# Revit family: FT Round Adjustable
name_source: partatom
category: Lighting Fixtures
revit_build: Autodesk Revit 2018 (Build: 20170927_1515(x64)
units: mm (PartAtom-declared; Revit-internal decimal feet)

## family parameters
Always vertical = Yes
Cut with Voids When Loaded = No
Host = Ceiling
Light Source = Yes
OmniClass Number = 23.80.70.11
OmniClass Title = Luminaries for Internal Lighting
Part Type = Normal
Room Calculation Point = No
Round Connector Dimension = Use Diameter
Shared = No

## types (2) — shared parameters
Color Filter = 16777215
Dimming Lamp Color Temperature Shift = <None>
Manufacturer URL - Europe and Rest of World = www.astrolighting.com
Manufacturer URL - North America = us.astrolighting.com
zero-valued in all types: Product Weight (KG)

## per-type parameters (varying)
| type | ADA compliant | Dimmable | Dimming Method | Driver Included | Driver Required | Efficacy (lm/w) | Electrical Class | Lamp | Length of supplied cable | Light Source Fixed | Location / IP Rating | Main Finish | Main Material | Photometric Web File | Power (Watts) | Product CCT | Product CRI | Product Location | Product Name | Product SKU | Tilt Angle |
| CE | Not Applicable | Yes | Control Gear Dependent | No | Yes | 72 | III | COB LED | 450mm | Yes | IP20 | White | Aluminium | Minima Round Fixed ALT LED Module.ies | 13.8 | 3000K | 90 | Indoor | Proform FT Round Adjustable | 1243005 | 30.00° |
| ETL |  |  |  |  |  |  |  |  |  |  |  |  |  | generic |  | 2700K / 3000K | 80/ 90 |  |  | 1234567 | 60.00° |

## geometry (parser evidence)
native form markers: Sweep x1
no freeform markers — native parametric forms only
